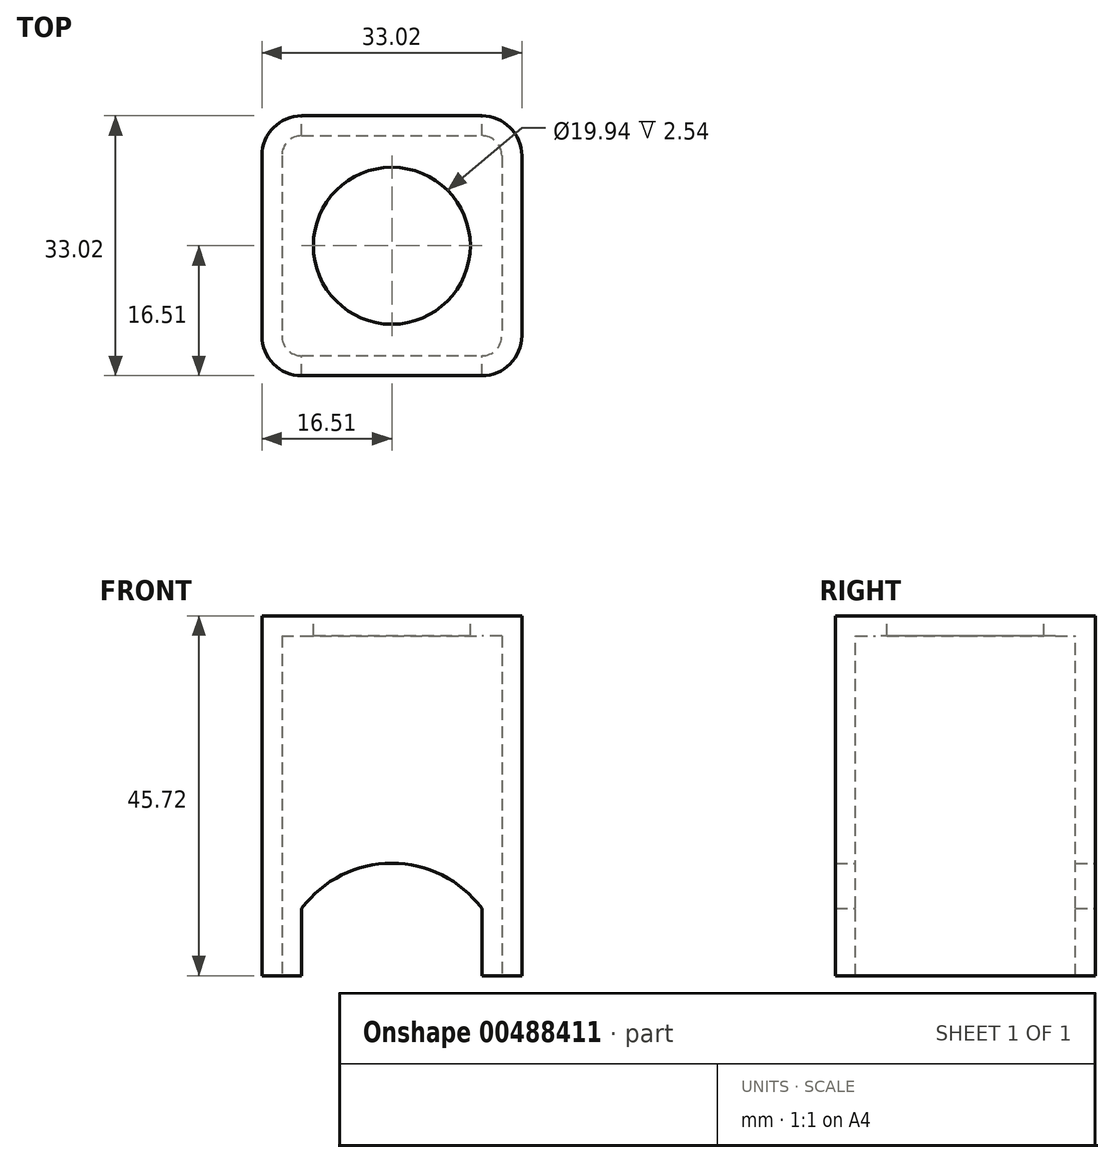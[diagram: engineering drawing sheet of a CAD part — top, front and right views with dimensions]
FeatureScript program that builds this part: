
annotation { "Feature Type Name" : "Feature", "Feature Type Description" : "" }
export const myFeature = defineFeature(function(context is Context, id is Id, definition is map)
    precondition{}
    {
        {
            var Q0;
            Q0=qCreatedBy(makeId("Top.planeOp"),FACE);
            var sketch = newSketch(context, id + "F0", { "sketchPlane" : qUnion([Q0])});
            skCircle(sketch, "E0", {"center": v(0, 0) * mm, "radius": 9.97 * mm});
            skLineSegment(sketch, "E1.bottom", {"start": v(-16.51, 16.51) * mm, "end": v(16.51, 16.51) * mm});
            skLineSegment(sketch, "E1.top", {"start": v(-16.51, -16.51) * mm, "end": v(16.51, -16.51) * mm});
            skLineSegment(sketch, "E1.left", {"start": v(-16.51, 16.51) * mm, "end": v(-16.51, -16.51) * mm});
            skLineSegment(sketch, "E1.right", {"start": v(16.51, 16.51) * mm, "end": v(16.51, -16.51) * mm});
            skSolve(sketch);
        }
        {
            var Q0;
            Q0 = qSketchRegion(id + "F0", true);
            var Q1;
            Q1=makeQuery(id+"F0.imprint","IMPRINT",FACE,{"disambiguationData":[TD([[makeQuery(id+"F0.imprint","IMPRINT",EDGE,{"derivedFrom":sQuery(id+"F0.wireOp",EDGE,"E0")}),1.0]])]});
            extrude(context, id + "F1", {"entities" : qUnion([Q0, Q1]), "depth" : 45.72 * mm});
        }
        {
            var Q0;
            Q0=makeQuery(id+"F1.opExtrude","SWEPT_EDGE",EDGE,{"disambiguationData":[OSD([sQuery(id+"F0.wireOp",EDGE,"E1.top"),sQuery(id+"F0.wireOp",EDGE,"E1.left")])]});
            var Q1;
            Q1=makeQuery(id+"F1.opExtrude","SWEPT_EDGE",EDGE,{"disambiguationData":[OSD([sQuery(id+"F0.wireOp",EDGE,"E1.top"),sQuery(id+"F0.wireOp",EDGE,"E1.right")])]});
            var Q2;
            Q2=makeQuery(id+"F1.opExtrude","SWEPT_EDGE",EDGE,{"disambiguationData":[OSD([sQuery(id+"F0.wireOp",EDGE,"E1.bottom"),sQuery(id+"F0.wireOp",EDGE,"E1.right")])]});
            var Q3;
            Q3=makeQuery(id+"F1.opExtrude","SWEPT_EDGE",EDGE,{"disambiguationData":[OSD([sQuery(id+"F0.wireOp",EDGE,"E1.bottom"),sQuery(id+"F0.wireOp",EDGE,"E1.left")])]});
            fillet(context, id + "F2", {"entities" : qUnion([Q0, Q1, Q2, Q3]), "radius" : 5.08 * mm, "tangentPropagation" : true, "allowEdgeOverflow" : false});
        }
        {
            var Q0;
            Q0=makeQuery(id+"F1.opExtrude","CAP_FACE",FACE,{"disambiguationData":[OSD([sQuery(id+"F0.wireOp",EDGE,"E0"),sQuery(id+"F0.wireOp",EDGE,"E1.bottom"),sQuery(id+"F0.wireOp",EDGE,"E1.top"),sQuery(id+"F0.wireOp",EDGE,"E1.left"),sQuery(id+"F0.wireOp",EDGE,"E1.right")])],"isStart":true});
            shell(context, id + "F3", {"entities" : qUnion([Q0]), "thickness" : 2.54 * mm});
        }
        {
            var Q0;
            Q0=makeQuery(id+"F1.opExtrude","CAP_FACE",FACE,{"disambiguationData":[OSD([sQuery(id+"F0.wireOp",EDGE,"E1.bottom"),sQuery(id+"F0.wireOp",EDGE,"E1.top"),sQuery(id+"F0.wireOp",EDGE,"E1.left"),sQuery(id+"F0.wireOp",EDGE,"E1.right")])],"isStart":false});
            var sketch = newSketch(context, id + "F4", { "sketchPlane" : qUnion([Q0])});
            skLineSegment(sketch, "E2", {"start": v(0, 39.25) * mm, "end": v(0, -52.7) * mm, "construction": true});
            skPoint(sketch, "E2.startSnap0", {"position": v(0, 16.51) * mm});
            skLineSegment(sketch, "E3", {"start": v(-57.64, 0) * mm, "end": v(56.69, 0) * mm, "construction": true});
            skPoint(sketch, "E4", {"position": v(0, 0) * mm});
            skSolve(sketch);
        }
        {
            var Q0;
            Q0=sQuery(id+"F4.wireOp",VERTEX,"E4");
            var Q1;
            Q1=makeQuery(id+"F1.opExtrude","SWEPT_BODY",BODY,{"disambiguationData":[OSD([sQuery(id+"F0.wireOp",EDGE,"E1.bottom"),sQuery(id+"F0.wireOp",EDGE,"E1.top"),sQuery(id+"F0.wireOp",EDGE,"E1.left"),sQuery(id+"F0.wireOp",EDGE,"E1.right")])]});
            hole(context, id + "F5", {"style" : HoleStyle.SIMPLE, "endStyle" : HoleEndStyle.THROUGH, "holeDiameter" : 19.94 * mm, "isTappedThrough" : true, "tappedDepth" : 12.7 * mm, "tapClearance" : 3, "locations" : qUnion([Q0]), "scope" : qUnion([Q1])});
        }
        {
            var Q0;
            Q0=makeQuery(id+"F1.opExtrude","SWEPT_FACE",FACE,{"disambiguationData":[OSD([sQuery(id+"F0.wireOp",EDGE,"E1.bottom")])]});
            var sketch = newSketch(context, id + "F6", { "sketchPlane" : qUnion([Q0])});
            skArc(sketch, "E5", {"start": v(14.29, 0) * mm, "mid": v(0, 14.29) * mm, "end": v(-14.29, 0) * mm});
            skLineSegment(sketch, "E6", {"start": v(-14.29, 0) * mm, "end": v(14.29, 0) * mm});
            skSolve(sketch);
        }
        {
            var Q0;
            {var subQ0=sQuery(id+"F6.wireOp",EDGE,"E6");var subQ1=sQuery(id+"F6.wireOp",EDGE,"E5");var subQ2=makeQuery(id+"F6.imprint","INTERSECT",VERTEX,{"disambiguationData":[OD(0.0)],"derivedFrom":[subQ1,subQ0]});Q0=makeQuery(id+"F6.imprint","IMPRINT",FACE,{"disambiguationData":[TD([[makeQuery(id+"F6.imprint","IMPRINT",EDGE,{"disambiguationData":[TD([[subQ2,-1.0]])],"derivedFrom":subQ1}),1.0]])]});}
            var Q1;
            {var subQ0=sQuery(id+"F6.wireOp",EDGE,"E6");var subQ1=sQuery(id+"F6.wireOp",EDGE,"E5");var subQ2=makeQuery(id+"F6.imprint","INTERSECT",VERTEX,{"disambiguationData":[OD(1.0)],"derivedFrom":[subQ1,subQ0]});Q1=makeQuery(id+"F6.imprint","IMPRINT",FACE,{"disambiguationData":[TD([[makeQuery(id+"F6.imprint","IMPRINT",EDGE,{"disambiguationData":[TD([[subQ2,1.0]])],"derivedFrom":subQ1}),1.0]])]});}
            var Q2;
            {var subQ0=sQuery(id+"F6.wireOp",EDGE,"E5");var subQ1=sQuery(id+"F0.wireOp",EDGE,"E1.bottom");var subQ2=makeQuery(id+"F1.opExtrude","SWEPT_FACE",FACE,{"disambiguationData":[OSD([subQ1])]});var subQ3=makeQuery(id+"F2.opFillet","BLEND_EDGE",EDGE,{"blendedFrom":[makeQuery(id+"F1.opExtrude","SWEPT_EDGE",EDGE,{"disambiguationData":[OSD([subQ1,sQuery(id+"F0.wireOp",EDGE,"E1.left")])]}),subQ2],"blendedInto":[subQ2]});var subQ4=makeQuery(id+"F6.imprint","INTERSECT",VERTEX,{"derivedFrom":[subQ3,subQ0]});Q2=makeQuery(id+"F6.imprint","IMPRINT",FACE,{"disambiguationData":[TD([[makeQuery(id+"F6.imprint","IMPRINT",EDGE,{"disambiguationData":[TD([[subQ4,-1.0]])],"derivedFrom":subQ0}),1.0]])]});}
            extrude(context, id + "F7", {"entities" : qUnion([Q0, Q1, Q2]), "operationType" : NewBodyOperationType.REMOVE, "endBound" : BoundingType.THROUGH_ALL, "oppositeDirection" : true, "depth" : 25.4 * mm});
        }
    });
